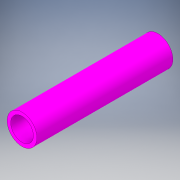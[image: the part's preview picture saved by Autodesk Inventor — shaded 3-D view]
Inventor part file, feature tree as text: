
AUTODESK INVENTOR PART (.ipt)
format: ipt  version: 2018.2 (Build 222227000, 227)  size: 107,520 bytes
history: native  units: in
note: dims shown in document units (in); Inventor stores cm internally (conversion verified against a paired STEP export)
features: extrude x1, sketch x1
ambient origin geometry x8: Origin, YZ Plane, XZ Plane, XY Plane, X Axis, Y Axis, Z Axis, Center Point
bodies: Solid1 (feature_tree)
feature tree (2):
  extrude  "Extrusion1"  Depth=6.0in
  sketch  "Sketch1"  dims[d0=1.315in d1=1.0in d2=6.0in d3=0.0in]
